# Revit family: Software_Event-Audience-Engagement_Biamp_Crowd-Mics
name_source: partatom
category: Communication Devices
units: mm (PartAtom-declared; Revit-internal decimal feet)

## family parameters
Cut with Voids When Loaded = No
Host = Face
Maintain Annotation Orientation = No
OmniClass Number = 23.85.10.11.14
OmniClass Title = Audio Equipment
Part Type = Normal
Room Calculation Point = No
Round Connector Dimension = Use Diameter
Shared = No

## types (1)
- Crowd Mics™
    Altitude = 0-10,000 ft (0-3000m) MSL
    Apparent Load = 132 VA
    Connector Description = 12V DC, 3.0A
    Current = 3 A
    D/A Converters = 24-bit
    Default Elevation = 48 "
    Depth = 5 "
    Description = Crowd Mics™ Audience Engagement Solution
    Dynamic Range (20Hz-20kHz, 0dB) = > 96dB
    Frequency Response (20Hz-20kHz, +4dBu) = +0/-0.25dB
    Height = 1 "
    Housing Material = Biamp - Plastic - Black
    Humidity = 0-95% relative humidity (non-condensing)
    Manufacturer = Biamp
    Max Power Consumption = 132 W
    Maximum Output = +12dBu
    Model = Crowd Mics™
    Network Connection = Gigabit Ethernet, RJ-45 (Cat 5 and above)
    Number of Outputs = 2
    Number of Poles = 1
    Output Impedance (balanced) = 200Ω
    Physical Interface = HDMI 2.0
    Physical Interface Analog Audio = Euroblock
    Power Factor = 1
    Product Documentation Link = https://downloads.biamp.com
    Product Page URL = https://www.biamp.com
    Product data url = https://bimobject.com
    Sampling Rate = 48 kHz
    Supported Resolutions = Up to 4K UHD
    THD+N (20Hz-20kHz) = < 0.006%
    Temperature Range = 32 - 95° F (0 - 35° C)
    URL = https://www.biamp.com
    Version = 1
    Voltage = 12 V
    Weight = 1.00 lb
    Width = 5 "

## geometry (parser evidence)
native form markers: Sweep x1
no freeform markers — native parametric forms only
